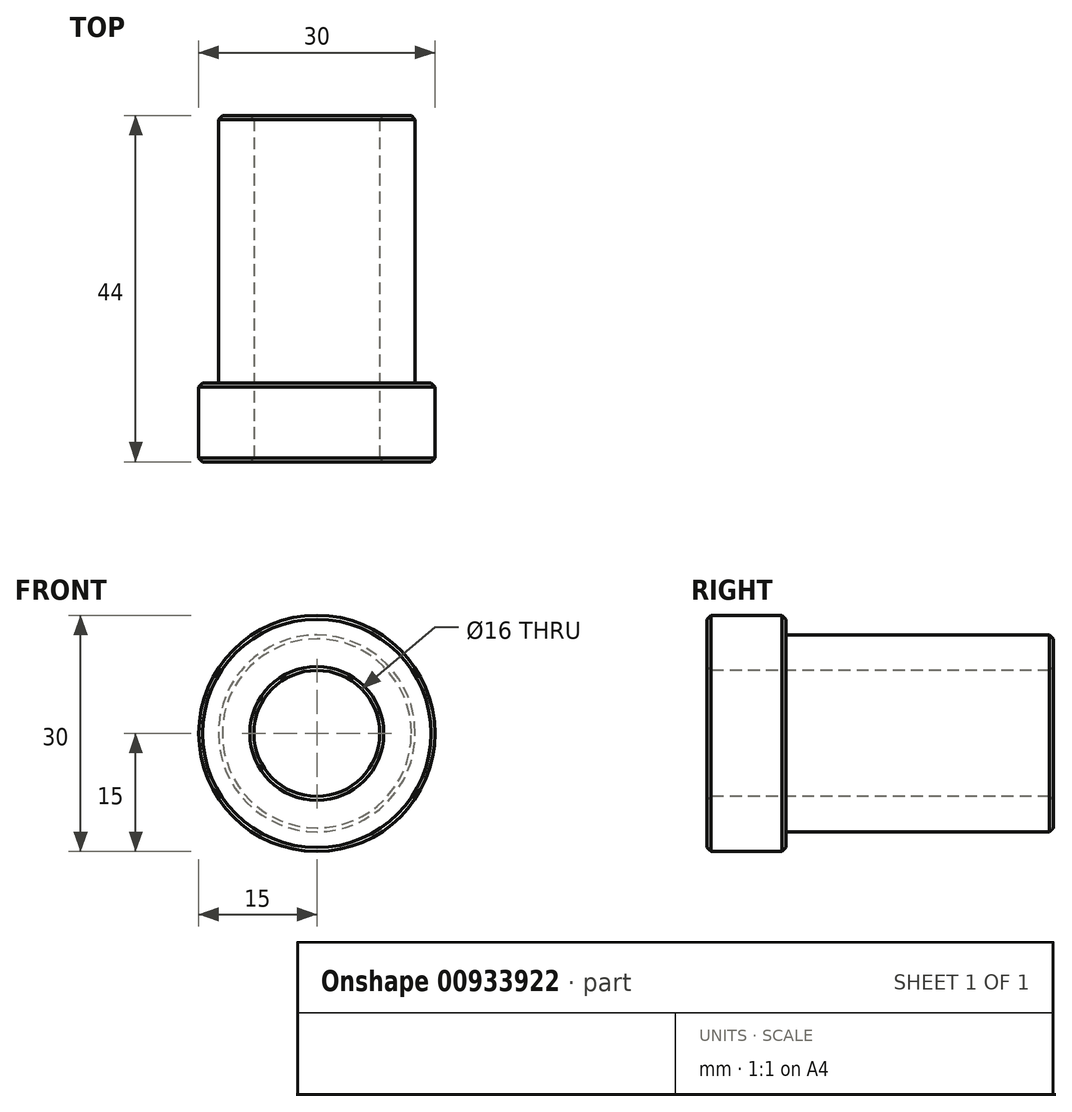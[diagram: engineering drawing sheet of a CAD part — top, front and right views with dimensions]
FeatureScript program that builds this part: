
annotation { "Feature Type Name" : "Feature", "Feature Type Description" : "" }
export const myFeature = defineFeature(function(context is Context, id is Id, definition is map)
    precondition{}
    {
        {
            var Q0;
            Q0=qCreatedBy(makeId("Front.planeOp"),FACE);
            var sketch = newSketch(context, id + "F0", { "sketchPlane" : qUnion([Q0])});
            skCircle(sketch, "E0", {"center": v(0, 0) * mm, "radius": 8 * mm});
            skCircle(sketch, "E1", {"center": v(0, 0) * mm, "radius": 12.5 * mm});
            skSolve(sketch);
        }
        {
            var Q0;
            Q0 = qSketchRegion(id + "F0", true);
            extrude(context, id + "F1", {"entities" : qUnion([Q0]), "oppositeDirection" : true, "depth" : 44 * mm, "offsetDistance" : 25 * mm});
        }
        {
            var Q0;
            Q0=qCreatedBy(makeId("Front.planeOp"),FACE);
            var sketch = newSketch(context, id + "F2", { "sketchPlane" : qUnion([Q0])});
            skCircle(sketch, "E2", {"center": v(0, 0) * mm, "radius": 15 * mm});
            skCircle(sketch, "E3", {"center": v(0, 0) * mm, "radius": 12.5 * mm});
            skSolve(sketch);
        }
        {
            var Q0;
            Q0 = qSketchRegion(id + "F2", true);
            extrude(context, id + "F3", {"entities" : qUnion([Q0]), "operationType" : NewBodyOperationType.ADD, "oppositeDirection" : true, "depth" : 10 * mm, "offsetDistance" : 25 * mm});
        }
        {
            var Q0;
            Q0=makeQuery(id+"F1.opExtrude","CAP_EDGE",EDGE,{"disambiguationData":[OSD([sQuery(id+"F0.wireOp",EDGE,"E0")])],"isStart":true});
            var Q1;
            Q1=makeQuery(id+"F3.opExtrude","CAP_EDGE",EDGE,{"disambiguationData":[OSD([sQuery(id+"F2.wireOp",EDGE,"E2")])],"isStart":true});
            var Q2;
            Q2=makeQuery(id+"F3.opExtrude","CAP_EDGE",EDGE,{"disambiguationData":[OSD([sQuery(id+"F2.wireOp",EDGE,"E2")])],"isStart":false});
            var Q3;
            Q3=makeQuery(id+"F1.opExtrude","CAP_EDGE",EDGE,{"disambiguationData":[OSD([sQuery(id+"F0.wireOp",EDGE,"E1")])],"isStart":false});
            var Q4;
            Q4=makeQuery(id+"F1.opExtrude","CAP_EDGE",EDGE,{"disambiguationData":[OSD([sQuery(id+"F0.wireOp",EDGE,"E0")])],"isStart":false});
            chamfer(context, id + "F4", {"entities" : qUnion([Q0, Q1, Q2, Q3, Q4]), "width" : .5 * mm, "tangentPropagation" : true});
        }
    });
